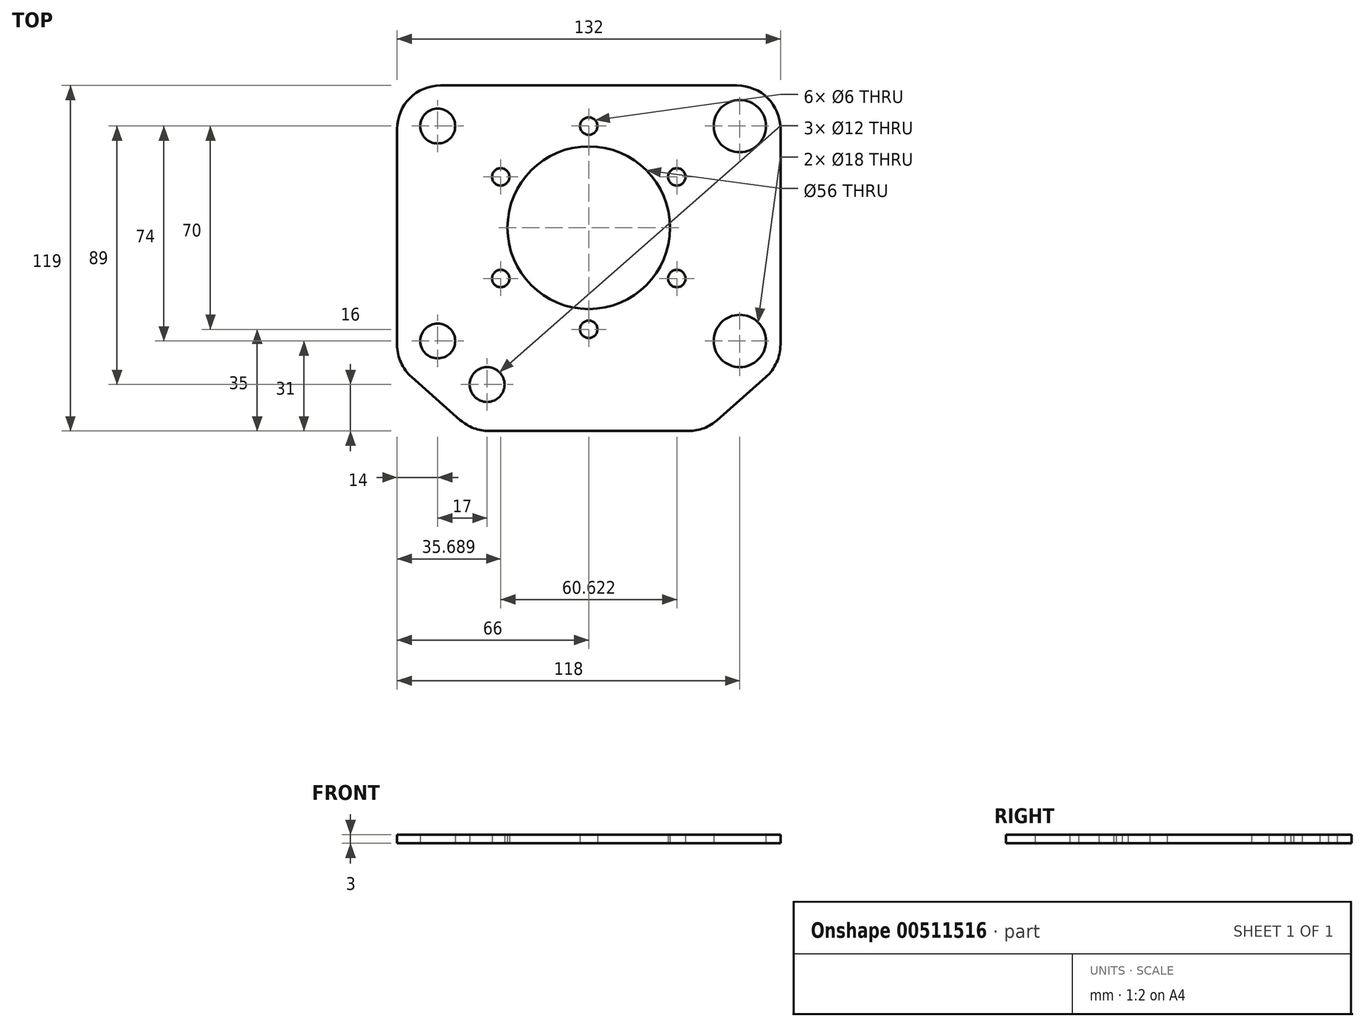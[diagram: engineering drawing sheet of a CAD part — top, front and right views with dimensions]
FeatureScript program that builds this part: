
annotation { "Feature Type Name" : "Feature", "Feature Type Description" : "" }
export const myFeature = defineFeature(function(context is Context, id is Id, definition is map)
    precondition{}
    {
        {
            var Q0;
            Q0=qCreatedBy(makeId("Top.planeOp"),FACE);
            var sketch = newSketch(context, id + "F0", { "sketchPlane" : qUnion([Q0])});
            skCircle(sketch, "E0", {"center": v(0, 0) * mm, "radius": 35 * mm});
            skCircle(sketch, "E1", {"center": v(0, 35) * mm, "radius": 3 * mm});
            skCircle(sketch, "E2", {"center": v(0, 0) * mm, "radius": 28 * mm});
            skCircle(sketch, "E3", {"center": v(0, 0) * mm, "radius": 49 * mm});
            skCircle(sketch, "E4", {"center": v(-52, 35) * mm, "radius": 9 * mm});
            skCircle(sketch, "E5", {"center": v(-52, 35) * mm, "radius": 6 * mm});
            skCircle(sketch, "E6", {"center": v(-52, -39) * mm, "radius": 9 * mm});
            skCircle(sketch, "E7", {"center": v(-52, -39) * mm, "radius": 6 * mm});
            skCircle(sketch, "E8.1.0.0", {"center": v(-35, -54) * mm, "radius": 9 * mm});
            skCircle(sketch, "E8.1.0.1", {"center": v(-35, -54) * mm, "radius": 6 * mm});
            skLineSegment(sketch, "E9", {"start": v(-66, 34) * mm, "end": v(-66, -40.24) * mm});
            skLineSegment(sketch, "E10", {"start": v(-51, 49) * mm, "end": v(0, 49) * mm});
            skCircle(sketch, "E11.1.0", {"center": v(-30.31, 17.5) * mm, "radius": 3 * mm});
            skCircle(sketch, "E11.2.0", {"center": v(-30.31, -17.5) * mm, "radius": 3 * mm});
            skCircle(sketch, "E11.3.0", {"center": v(0, -35) * mm, "radius": 3 * mm});
            skCircle(sketch, "E11.4.0", {"center": v(30.31, -17.5) * mm, "radius": 3 * mm});
            skCircle(sketch, "E11.5.0", {"center": v(30.31, 17.5) * mm, "radius": 3 * mm});
            skLineSegment(sketch, "E12", {"start": v(-60.94, -51.48) * mm, "end": v(-44.26, -66.23) * mm});
            skLineSegment(sketch, "E13", {"start": v(-34.32, -70) * mm, "end": v(0, -70) * mm});
            skLineSegment(sketch, "E14", {"start": v(0, 0) * mm, "end": v(0, -70) * mm});
            skCircle(sketch, "E15.MirrorC", {"center": v(35, -54) * mm, "radius": 6 * mm});
            skCircle(sketch, "E16.MirrorC", {"center": v(35, -54) * mm, "radius": 9 * mm});
            skCircle(sketch, "E17.MirrorC", {"center": v(52, -39) * mm, "radius": 9 * mm});
            skCircle(sketch, "E18.MirrorC", {"center": v(52, -39) * mm, "radius": 6 * mm});
            skCircle(sketch, "E19.MirrorC", {"center": v(52, 35) * mm, "radius": 9 * mm});
            skCircle(sketch, "E20.MirrorC", {"center": v(52, 35) * mm, "radius": 6 * mm});
            skPoint(sketch, "E21.visualSharp", {"position": v(-66, 49) * mm});
            skArc(sketch, "E21.filletArc", {"start": v(-51, 49) * mm, "mid": v(-61.6, 44.6) * mm, "end": v(-66, 34) * mm});
            skLineSegment(sketch, "E22.MirrorCS", {"start": v(-81, 49) * mm, "end": v(-132, 49) * mm});
            skLineSegment(sketch, "E23.MirrorCS", {"start": v(51, 49) * mm, "end": v(0, 49) * mm});
            skArc(sketch, "E24.MirrorCS", {"start": v(51, 49) * mm, "mid": v(61.6, 44.6) * mm, "end": v(66, 34) * mm});
            skPoint(sketch, "E25.visualSharp", {"position": v(-66, -47) * mm});
            skArc(sketch, "E25.filletArc", {"start": v(-66, -40.24) * mm, "mid": v(-64.68, -46.4) * mm, "end": v(-60.94, -51.48) * mm});
            skPoint(sketch, "E26.visualSharp", {"position": v(-40, -70) * mm});
            skArc(sketch, "E26.filletArc", {"start": v(-44.26, -66.23) * mm, "mid": v(-39.63, -69.03) * mm, "end": v(-34.32, -70) * mm});
            skLineSegment(sketch, "E27.MirrorCS", {"start": v(34.32, -70) * mm, "end": v(0, -70) * mm});
            skArc(sketch, "E28.MirrorCS", {"start": v(44.26, -66.23) * mm, "mid": v(39.63, -69.03) * mm, "end": v(34.32, -70) * mm});
            skLineSegment(sketch, "E29.MirrorCS", {"start": v(60.94, -51.48) * mm, "end": v(44.26, -66.23) * mm});
            skArc(sketch, "E30.MirrorCS", {"start": v(66, -40.24) * mm, "mid": v(64.68, -46.4) * mm, "end": v(60.94, -51.48) * mm});
            skLineSegment(sketch, "E31.MirrorCS", {"start": v(66, 34) * mm, "end": v(66, -40.24) * mm});
            skSolve(sketch);
        }
        {
            var Q0;
            Q0=makeQuery(id+"F0.imprint","IMPRINT",FACE,{"disambiguationData":[TD([[makeQuery(id+"F0.imprint","IMPRINT",EDGE,{"derivedFrom":sQuery(id+"F0.wireOp",EDGE,"E4")}),-1.0]])]});
            var Q1;
            {var subQ3=sQuery(id+"F0.wireOp",EDGE,"E0");var subQ7=sQuery(id+"F0.wireOp",EDGE,"58bc0455-ba74-4933-bc44-42c9ffa78a9b.5.0");var subQ10=makeQuery(id+"F0.imprint","INTERSECT",VERTEX,{"disambiguationData":[OD(0.0)],"derivedFrom":[subQ3,subQ7]});Q1=makeQuery(id+"F0.imprint","IMPRINT",FACE,{"disambiguationData":[TD([[makeQuery(id+"F0.imprint","IMPRINT",EDGE,{"disambiguationData":[TD([[subQ10,-1.0]])],"derivedFrom":subQ3}),-1.0]])]});}
            var Q2;
            Q2=makeQuery(id+"F0.imprint","IMPRINT",FACE,{"disambiguationData":[TD([[makeQuery(id+"F0.imprint","IMPRINT",EDGE,{"derivedFrom":sQuery(id+"F0.wireOp",EDGE,"E2")}),-1.0]])]});
            var Q3;
            Q3=makeQuery(id+"F0.imprint","IMPRINT",FACE,{"disambiguationData":[TD([[makeQuery(id+"F0.imprint","IMPRINT",EDGE,{"derivedFrom":sQuery(id+"F0.wireOp",EDGE,"E4")}),1.0]])]});
            var Q4;
            Q4=makeQuery(id+"F0.imprint","IMPRINT",FACE,{"disambiguationData":[TD([[makeQuery(id+"F0.imprint","IMPRINT",EDGE,{"derivedFrom":sQuery(id+"F0.wireOp",EDGE,"E6")}),1.0]])]});
            var Q5;
            Q5=makeQuery(id+"F0.imprint","IMPRINT",FACE,{"disambiguationData":[TD([[makeQuery(id+"F0.imprint","IMPRINT",EDGE,{"derivedFrom":sQuery(id+"F0.wireOp",EDGE,"E8.1.0.0")}),1.0]])]});
            var Q6;
            Q6=makeQuery(id+"F0.imprint","IMPRINT",FACE,{"disambiguationData":[TD([[makeQuery(id+"F0.imprint","IMPRINT",EDGE,{"derivedFrom":sQuery(id+"F0.wireOp",EDGE,"2309bc13-186c-4cf0-9cfe-caf2748ff36a1.MirrorC")}),1.0]])]});
            var Q7;
            Q7=makeQuery(id+"F0.imprint","IMPRINT",FACE,{"disambiguationData":[TD([[makeQuery(id+"F0.imprint","IMPRINT",EDGE,{"derivedFrom":sQuery(id+"F0.wireOp",EDGE,"2309bc13-186c-4cf0-9cfe-caf2748ff36a0.MirrorC")}),1.0]])]});
            var Q8;
            Q8=makeQuery(id+"F0.imprint","IMPRINT",FACE,{"disambiguationData":[TD([[makeQuery(id+"F0.imprint","IMPRINT",EDGE,{"derivedFrom":sQuery(id+"F0.wireOp",EDGE,"2309bc13-186c-4cf0-9cfe-caf2748ff36a2.MirrorC")}),-1.0]])]});
            var Q9;
            Q9=makeQuery(id+"F0.imprint","IMPRINT",FACE,{"disambiguationData":[TD([[makeQuery(id+"F0.imprint","IMPRINT",EDGE,{"derivedFrom":sQuery(id+"F0.wireOp",EDGE,"2309bc13-186c-4cf0-9cfe-caf2748ff36a4.MirrorC")}),-1.0]])]});
            var Q10;
            {var subQ5=sQuery(id+"F0.wireOp",EDGE,"E0");var subQ11=sQuery(id+"F0.wireOp",EDGE,"E11.5.0");var subQ14=makeQuery(id+"F0.imprint","INTERSECT",VERTEX,{"disambiguationData":[OD(0.0)],"derivedFrom":[subQ5,subQ11]});Q10=makeQuery(id+"F0.imprint","IMPRINT",FACE,{"disambiguationData":[TD([[makeQuery(id+"F0.imprint","IMPRINT",EDGE,{"disambiguationData":[TD([[subQ14,-1.0]])],"derivedFrom":subQ5}),-1.0]])]});}
            var Q11;
            {var subQ0=sQuery(id+"F0.wireOp",EDGE,"ed007a0e-1ac5-4646-8f30-e8137fff68850.MirrorCS");Q11=makeQuery(id+"F0.imprint","IMPRINT",FACE,{"disambiguationData":[TD([[makeQuery(id+"F0.imprint","IMPRINT",EDGE,{"derivedFrom":subQ0}),-1.0]])]});}
            var Q12;
            Q12=makeQuery(id+"F0.imprint","IMPRINT",FACE,{"disambiguationData":[TD([[makeQuery(id+"F0.imprint","IMPRINT",EDGE,{"derivedFrom":sQuery(id+"F0.wireOp",EDGE,"E15.MirrorC")}),1.0]])]});
            var Q13;
            Q13=makeQuery(id+"F0.imprint","IMPRINT",FACE,{"disambiguationData":[TD([[makeQuery(id+"F0.imprint","IMPRINT",EDGE,{"derivedFrom":sQuery(id+"F0.wireOp",EDGE,"E17.MirrorC")}),-1.0]])]});
            var Q14;
            Q14=makeQuery(id+"F0.imprint","IMPRINT",FACE,{"disambiguationData":[TD([[makeQuery(id+"F0.imprint","IMPRINT",EDGE,{"derivedFrom":sQuery(id+"F0.wireOp",EDGE,"E19.MirrorC")}),-1.0]])]});
            var Q15;
            Q15=makeQuery(id+"F0.imprint","IMPRINT",FACE,{"disambiguationData":[TD([[makeQuery(id+"F0.imprint","IMPRINT",EDGE,{"derivedFrom":sQuery(id+"F0.wireOp",EDGE,"E16.MirrorC")}),1.0]])]});
            extrude(context, id + "F1", {"entities" : qUnion([Q0, Q1, Q2, Q3, Q4, Q5, Q6, Q7, Q8, Q9, Q10, Q11, Q12, Q13, Q14, Q15]), "depth" : 3 * mm, "offsetDistance" : 25 * mm});
        }
    });
